# Revit family: UNO
name_source: partatom
category: Wyposażenie mechaniczne
revit_build: Autodesk Revit 2017 (Build: 20160225_1515(x64)
units: mm (PartAtom-declared; Revit-internal decimal feet)

## family parameters
Oparty na płaszczyźnie roboczej = Nie
Punkt obliczania pomieszczeń = Nie
Tnij formami wycięć po wczytaniu = Nie
Typ części = Normalny
Współdzielony = Nie
Wymiar okrągłego złącza = Użyj średnicy
Zawsze pionowo = Tak

## types (17) — shared parameters
Date = 11.2018
Frequency = 50 Hz
Producent = Rosenberg
URL = https://www.rosenberg.pl
Version = 1

## per-type parameters (varying)
| type | A_ABH | A_ELS | A_JKL | A_WSD | Air_flow | B_ABH | B_ELS | B_GR | B_JKL | B_WSD | C_ELS | Current | Diameter | H_FUS | Height | L_FUS | Logo_scale | Power | Pressure | Protection_class | Voltage | Weight[kg] | Width | max.Ambient_temperature |
| 50-315-4E.3EF | 300 mm  [stored 0.984252 ft] | 409 mm  [stored 1.34186 ft] | 339 mm  [stored 1.1122 ft] | 600 mm | 1036.0 m³/h | 450 mm  [stored 1.47638 ft] | 433 mm | 464 mm  [stored 1.52231 ft] | 363 mm | 720 mm  [stored 2.3622 ft] | 20 mm  [stored 0.0656168 ft] | 1 A | 203 mm  [stored 0.66601 ft] | 32 mm  [stored 0.104987 ft] | 500 mm  [stored 1.64042 ft] | 600 mm | 1 mm  [stored 0.00328084 ft] | 0 kW | 147.0 Pa | IP44 | 230 V | 31 | 500 mm  [stored 1.64042 ft] | 70 °C |
| 50-355-4E.5FA | 300 mm  [stored 0.984252 ft] | 409 mm  [stored 1.34186 ft] | 339 mm  [stored 1.1122 ft] | 600 mm | 1931.0 m³/h | 450 mm  [stored 1.47638 ft] | 433 mm | 464 mm  [stored 1.52231 ft] | 363 mm | 720 mm  [stored 2.3622 ft] | 20 mm  [stored 0.0656168 ft] | 1 A | 228 mm  [stored 0.748031 ft] | 32 mm  [stored 0.104987 ft] | 500 mm  [stored 1.64042 ft] | 600 mm | 1 mm  [stored 0.00328084 ft] | 0 kW | 256.0 Pa | IP54 | 230 V | 32 | 500 mm  [stored 1.64042 ft] | 65 °C |
| 67-400-4E.5HA | 380 mm | 579 mm  [stored 1.89961 ft] | 509 mm  [stored 1.66995 ft] | 770 mm | 2888.0 m³/h | 620 mm  [stored 2.03412 ft] | 633 mm  [stored 2.07677 ft] | 634 mm  [stored 2.08005 ft] | 563 mm  [stored 1.84711 ft] | 800 mm | 20 mm  [stored 0.0656168 ft] | 2 A | 257 mm  [stored 0.843176 ft] | 32 mm  [stored 0.104987 ft] | 620 mm  [stored 2.03412 ft] | 770 mm | 2 mm  [stored 0.00656168 ft] | 1 kW | 316.0 Pa | IP54 | 230 V | 32 | 670 mm  [stored 2.19816 ft] | 65 °C |
| 67-450-4E.6FA | 380 mm | 579 mm  [stored 1.89961 ft] | 509 mm  [stored 1.66995 ft] | 770 mm | 4182.0 m³/h | 620 mm  [stored 2.03412 ft] | 633 mm  [stored 2.07677 ft] | 634 mm  [stored 2.08005 ft] | 563 mm  [stored 1.84711 ft] | 800 mm | 20 mm  [stored 0.0656168 ft] | 1 A | 289 mm  [stored 0.948163 ft] | 32 mm  [stored 0.104987 ft] | 620 mm  [stored 2.03412 ft] | 770 mm | 2 mm  [stored 0.00656168 ft] | 1 kW | 403.0 Pa | IP54 | 230 V | 60 | 670 mm  [stored 2.19816 ft] | 45 °C |
| 80-500-4E.6HF | 430 mm | 659 mm  [stored 2.16207 ft] | 589 mm | 900 mm | 5639.0 m³/h | 720 mm  [stored 2.3622 ft] | 697 mm  [stored 2.28675 ft] | 764 mm  [stored 2.50656 ft] | 627 mm  [stored 2.05709 ft] | 890 mm | 30 mm  [stored 0.0984252 ft] | 6 A | 325 mm  [stored 1.06627 ft] | 53 mm | 720 mm  [stored 2.3622 ft] | 900 mm | 2 mm  [stored 0.00656168 ft] | 1 kW | 480.0 Pa | IP54 | 230 V | 85 | 800 mm | 40 °C |
| 102-710-6D.7NA | 520 mm  [stored 1.70604 ft] | 879 mm | 809 mm | 1120 mm | 9316.0 m³/h | 940 mm | 917 mm | 984 mm | 847 mm | 1180 mm | 30 mm  [stored 0.0984252 ft] | 5 A | 460 mm  [stored 1.50919 ft] | 53 mm | 940 mm | 1120 mm | 2 mm  [stored 0.00656168 ft] | 2 kW | 480.0 Pa | IP54 | 400 V | 160 | 1020 mm | 70 °C |
| 80-560-4D.6LA | 430 mm | 659 mm  [stored 2.16207 ft] | 589 mm | 900 mm | 8030.0 m³/h | 720 mm  [stored 2.3622 ft] | 697 mm  [stored 2.28675 ft] | 764 mm  [stored 2.50656 ft] | 627 mm  [stored 2.05709 ft] | 1040 mm | 30 mm  [stored 0.0984252 ft] | 4 A | 365 mm  [stored 1.19751 ft] | 53 mm | 800 mm | 900 mm | 2 mm  [stored 0.00656168 ft] | 2 kW | 548.0 Pa | IP54 | 400 V | 95 | 800 mm | 50 °C |
| 67-500-4E.6HF | 380 mm | 579 mm  [stored 1.89961 ft] | 509 mm  [stored 1.66995 ft] | 770 mm | 5781.0 m³/h | 620 mm  [stored 2.03412 ft] | 633 mm  [stored 2.07677 ft] | 634 mm  [stored 2.08005 ft] | 563 mm  [stored 1.84711 ft] | 800 mm | 20 mm  [stored 0.0656168 ft] | 6 A | 325 mm  [stored 1.06627 ft] | 32 mm  [stored 0.104987 ft] | 620 mm  [stored 2.03412 ft] | 770 mm | 2 mm  [stored 0.00656168 ft] | 1 kW | 461.0 Pa | IP54 | 230 V | 62 | 670 mm  [stored 2.19816 ft] | 40 °C |
| 50-355-4D.5DF | 300 mm  [stored 0.984252 ft] | 409 mm  [stored 1.34186 ft] | 339 mm  [stored 1.1122 ft] | 600 mm | 1877.0 m³/h | 450 mm  [stored 1.47638 ft] | 433 mm | 464 mm  [stored 1.52231 ft] | 363 mm | 720 mm  [stored 2.3622 ft] | 20 mm  [stored 0.0656168 ft] | 1 A | 228 mm  [stored 0.748031 ft] | 32 mm  [stored 0.104987 ft] | 500 mm  [stored 1.64042 ft] | 600 mm | 1 mm  [stored 0.00328084 ft] | 0 kW | 254.0 Pa | IP54 | 400 V | 32 | 500 mm  [stored 1.64042 ft] | 70 °C |
| 67-400-4D.5FA | 380 mm | 579 mm  [stored 1.89961 ft] | 509 mm  [stored 1.66995 ft] | 770 mm | 282.0 m³/h | 620 mm  [stored 2.03412 ft] | 633 mm  [stored 2.07677 ft] | 634 mm  [stored 2.08005 ft] | 563 mm  [stored 1.84711 ft] | 800 mm | 20 mm  [stored 0.0656168 ft] | 1 A | 257 mm  [stored 0.843176 ft] | 32 mm  [stored 0.104987 ft] | 620 mm  [stored 2.03412 ft] | 770 mm | 2 mm  [stored 0.00656168 ft] | 0 kW | 297.0 Pa | IP54 | 400 V | 32 | 670 mm  [stored 2.19816 ft] | 70 °C |
| 67-450-4D.5HA | 380 mm | 579 mm  [stored 1.89961 ft] | 509 mm  [stored 1.66995 ft] | 770 mm | 4048.0 m³/h | 620 mm  [stored 2.03412 ft] | 633 mm  [stored 2.07677 ft] | 634 mm  [stored 2.08005 ft] | 563 mm  [stored 1.84711 ft] | 800 mm | 20 mm  [stored 0.0656168 ft] | 1 A | 286 mm | 32 mm  [stored 0.104987 ft] | 620 mm  [stored 2.03412 ft] | 770 mm | 2 mm  [stored 0.00656168 ft] | 1 kW | 350.0 Pa | IP54 | 400 V | 50 | 670 mm  [stored 2.19816 ft] | 55 °C |
| 67-500-4D.6HF | 380 mm | 579 mm  [stored 1.89961 ft] | 509 mm  [stored 1.66995 ft] | 770 mm | 5808.0 m³/h | 620 mm  [stored 2.03412 ft] | 633 mm  [stored 2.07677 ft] | 634 mm  [stored 2.08005 ft] | 563 mm  [stored 1.84711 ft] | 800 mm | 20 mm  [stored 0.0656168 ft] | 3 A | 325 mm  [stored 1.06627 ft] | 32 mm  [stored 0.104987 ft] | 620 mm  [stored 2.03412 ft] | 770 mm | 2 mm  [stored 0.00656168 ft] | 1 kW | 459.0 Pa | IP54 | 400 V | 62 | 670 mm  [stored 2.19816 ft] | 60 °C |
| 67-500-6D.6DF | 380 mm | 579 mm  [stored 1.89961 ft] | 509 mm  [stored 1.66995 ft] | 770 mm | 3532.0 m³/h | 620 mm  [stored 2.03412 ft] | 633 mm  [stored 2.07677 ft] | 634 mm  [stored 2.08005 ft] | 563 mm  [stored 1.84711 ft] | 800 mm | 20 mm  [stored 0.0656168 ft] | 1 A | 325 mm  [stored 1.06627 ft] | 32 mm  [stored 0.104987 ft] | 620 mm  [stored 2.03412 ft] | 770 mm | 2 mm  [stored 0.00656168 ft] | 0 kW | 210.0 Pa | IP54 | 400 V | 60 | 670 mm  [stored 2.19816 ft] | 65 °C |
| 80-500-4D.6HF | 430 mm | 659 mm  [stored 2.16207 ft] | 589 mm | 900 mm | 5732.0 m³/h | 720 mm  [stored 2.3622 ft] | 697 mm  [stored 2.28675 ft] | 764 mm  [stored 2.50656 ft] | 627 mm  [stored 2.05709 ft] | 890 mm | 30 mm  [stored 0.0984252 ft] | 3 A | 325 mm  [stored 1.06627 ft] | 53 mm | 720 mm  [stored 2.3622 ft] | 900 mm | 2 mm  [stored 0.00656168 ft] | 1 kW | 495.0 Pa | IP54 | 400 V | 85 | 800 mm | 70 °C |
| 80-560-6D.6FA | 430 mm | 659 mm  [stored 2.16207 ft] | 589 mm | 900 mm | 4869.0 m³/h | 720 mm  [stored 2.3622 ft] | 697 mm  [stored 2.28675 ft] | 764 mm  [stored 2.50656 ft] | 627 mm  [stored 2.05709 ft] | 1040 mm | 30 mm  [stored 0.0984252 ft] | 2 A | 325 mm  [stored 1.06627 ft] | 53 mm | 720 mm  [stored 2.3622 ft] | 900 mm | 2 mm  [stored 0.00656168 ft] | 1 kW | 254.0 Pa | IP54 | 400 V | 85 | 800 mm | 70 °C |
| 80-630-4D.7NA | 430 mm | 659 mm  [stored 2.16207 ft] | 589 mm | 900 mm | 8100.0 m³/h | 720 mm  [stored 2.3622 ft] | 697 mm  [stored 2.28675 ft] | 764 mm  [stored 2.50656 ft] | 627 mm  [stored 2.05709 ft] | 1040 mm | 30 mm  [stored 0.0984252 ft] | 6 A | 410 mm  [stored 1.34514 ft] | 53 mm | 720 mm  [stored 2.3622 ft] | 900 mm | 2 mm  [stored 0.00656168 ft] | 3 kW | 800.0 Pa | IP54 | 400 V | 105 | 800 mm | 60 °C |
| 80-630-6D.7HF | 430 mm | 659 mm  [stored 2.16207 ft] | 589 mm | 900 mm | 5624.0 m³/h | 720 mm  [stored 2.3622 ft] | 697 mm  [stored 2.28675 ft] | 764 mm  [stored 2.50656 ft] | 627 mm  [stored 2.05709 ft] | 1040 mm | 30 mm  [stored 0.0984252 ft] | 2 A | 410 mm  [stored 1.34514 ft] | 53 mm | 720 mm  [stored 2.3622 ft] | 900 mm | 2 mm  [stored 0.00656168 ft] | 1 kW | 328.0 Pa | IP54 | 400 V | 86 | 800 mm | 70 °C |

note: column(s) folded — value = type name in every type: Model

note: [stored X ft] marks values corroborated as IEEE doubles in the binary element streams (Revit-internal decimal feet)
